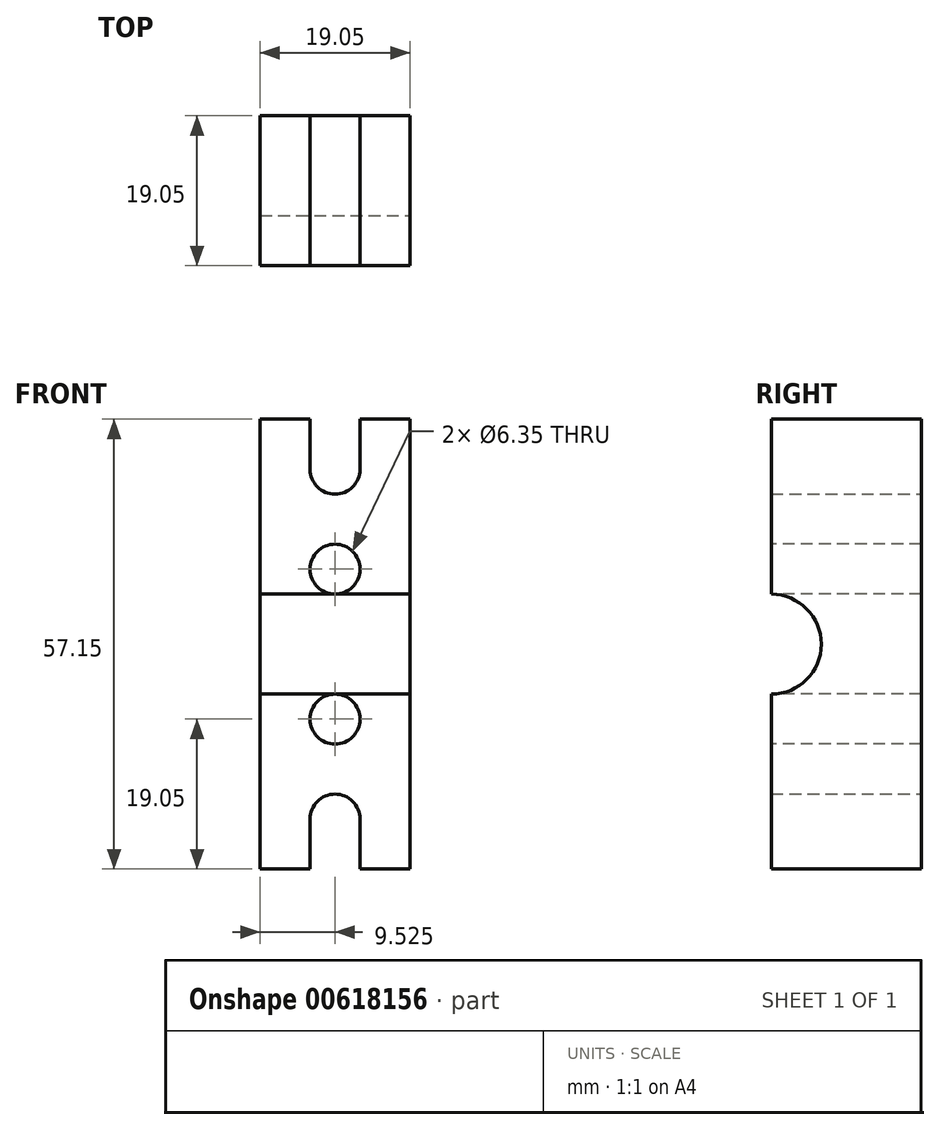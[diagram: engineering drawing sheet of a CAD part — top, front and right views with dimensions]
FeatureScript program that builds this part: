
annotation { "Feature Type Name" : "Feature", "Feature Type Description" : "" }
export const myFeature = defineFeature(function(context is Context, id is Id, definition is map)
    precondition{}
    {
        {
            var Q0;
            Q0=qCreatedBy(makeId("Front.planeOp"),FACE);
            var sketch = newSketch(context, id + "F0", { "sketchPlane" : qUnion([Q0])});
            skLineSegment(sketch, "E0.bottom", {"start": v(0, 0) * mm, "end": v(19.05, 0) * mm});
            skLineSegment(sketch, "E0.top", {"start": v(0, 57.15) * mm, "end": v(19.05, 57.15) * mm});
            skLineSegment(sketch, "E0.left", {"start": v(0, 0) * mm, "end": v(0, 57.15) * mm});
            skLineSegment(sketch, "E0.right", {"start": v(19.05, 0) * mm, "end": v(19.05, 57.15) * mm});
            skLineSegment(sketch, "E1.bottom", {"start": v(12.7, 50.8) * mm, "end": v(6.35, 50.8) * mm});
            skLineSegment(sketch, "E1.top", {"start": v(12.7, 63.5) * mm, "end": v(6.35, 63.5) * mm});
            skLineSegment(sketch, "E1.left", {"start": v(12.7, 50.8) * mm, "end": v(12.7, 63.5) * mm});
            skLineSegment(sketch, "E1.right", {"start": v(6.35, 50.8) * mm, "end": v(6.35, 63.5) * mm});
            skPoint(sketch, "E1.middle", {"position": v(9.52, 57.15) * mm});
            skCircle(sketch, "E2", {"center": v(9.52, 50.8) * mm, "radius": 3.18 * mm});
            skLineSegment(sketch, "E3.bottom", {"start": v(12.7, -6.35) * mm, "end": v(6.35, -6.35) * mm});
            skLineSegment(sketch, "E3.top", {"start": v(12.7, 6.35) * mm, "end": v(6.35, 6.35) * mm});
            skLineSegment(sketch, "E3.left", {"start": v(12.7, -6.35) * mm, "end": v(12.7, 6.35) * mm});
            skLineSegment(sketch, "E3.right", {"start": v(6.35, -6.35) * mm, "end": v(6.35, 6.35) * mm});
            skPoint(sketch, "E3.middle", {"position": v(9.53, 0) * mm});
            skCircle(sketch, "E4", {"center": v(9.53, 6.35) * mm, "radius": 3.17 * mm});
            skSolve(sketch);
        }
        {
            var Q0;
            {var subQ16=sQuery(id+"F0.wireOp",EDGE,"E0.left");Q0=makeQuery(id+"F0.imprint","IMPRINT",FACE,{"disambiguationData":[TD([[makeQuery(id+"F0.imprint","IMPRINT",EDGE,{"derivedFrom":subQ16}),-1.0]])]});}
            extrude(context, id + "F1", {"entities" : qUnion([Q0]), "depth" : 19.05 * mm});
        }
        {
            var Q0;
            Q0=makeQuery(id+"F1.opExtrude","CAP_FACE",FACE,{"disambiguationData":[OSD([sQuery(id+"F0.wireOp",EDGE,"E0.bottom"),sQuery(id+"F0.wireOp",EDGE,"E0.top"),sQuery(id+"F0.wireOp",EDGE,"E0.left"),sQuery(id+"F0.wireOp",EDGE,"E0.right"),sQuery(id+"F0.wireOp",EDGE,"E1.left"),sQuery(id+"F0.wireOp",EDGE,"E1.right"),sQuery(id+"F0.wireOp",EDGE,"E2"),sQuery(id+"F0.wireOp",EDGE,"E3.left"),sQuery(id+"F0.wireOp",EDGE,"E3.right"),sQuery(id+"F0.wireOp",EDGE,"E4")])],"isStart":false});
            var sketch = newSketch(context, id + "F2", { "sketchPlane" : qUnion([Q0])});
            skLineSegment(sketch, "E5", {"start": v(0, 0) * mm, "end": v(19.05, 57.15) * mm, "construction": true});
            skLineSegment(sketch, "E6.bottom", {"start": v(19.05, 12.7) * mm, "end": v(0, 12.7) * mm});
            skLineSegment(sketch, "E6.top", {"start": v(19.05, 44.45) * mm, "end": v(0, 44.45) * mm});
            skLineSegment(sketch, "E6.left", {"start": v(19.05, 12.7) * mm, "end": v(19.05, 44.45) * mm});
            skLineSegment(sketch, "E6.right", {"start": v(0, 12.7) * mm, "end": v(0, 44.45) * mm});
            skPoint(sketch, "E6.middle", {"position": v(9.52, 28.58) * mm});
            skLineSegment(sketch, "E7", {"start": v(9.52, 44.45) * mm, "end": v(9.52, 12.7) * mm, "construction": true});
            skCircle(sketch, "E8", {"center": v(9.52, 38.1) * mm, "radius": 3.17 * mm});
            skCircle(sketch, "E9", {"center": v(9.53, 19.05) * mm, "radius": 3.18 * mm});
            skSolve(sketch);
        }
        {
            var Q0;
            Q0=makeQuery(id+"F2.imprint","IMPRINT",FACE,{"disambiguationData":[TD([[makeQuery(id+"F2.imprint","IMPRINT",EDGE,{"derivedFrom":sQuery(id+"F2.wireOp",EDGE,"E8")}),1.0]])]});
            var Q1;
            Q1=makeQuery(id+"F2.imprint","IMPRINT",FACE,{"disambiguationData":[TD([[makeQuery(id+"F2.imprint","IMPRINT",EDGE,{"derivedFrom":sQuery(id+"F2.wireOp",EDGE,"E9")}),1.0]])]});
            extrude(context, id + "F3", {"entities" : qUnion([Q0, Q1]), "operationType" : NewBodyOperationType.REMOVE, "endBound" : BoundingType.THROUGH_ALL, "oppositeDirection" : true, "depth" : 25.4 * mm});
        }
        {
            var Q0;
            Q0=makeQuery(id+"F1.opExtrude","SWEPT_FACE",FACE,{"disambiguationData":[OSD([sQuery(id+"F0.wireOp",EDGE,"E0.right")])]});
            var sketch = newSketch(context, id + "F4", { "sketchPlane" : qUnion([Q0])});
            skCircle(sketch, "E10", {"center": v(-19.05, 28.57) * mm, "radius": 6.35 * mm});
            skSolve(sketch);
        }
        {
            var Q0;
            Q0=qSketchRegion(id+"F4",true);
            extrude(context, id + "F5", {"entities" : qUnion([Q0]), "operationType" : NewBodyOperationType.REMOVE, "endBound" : BoundingType.THROUGH_ALL, "oppositeDirection" : true, "depth" : 25.4 * mm});
        }
    });
